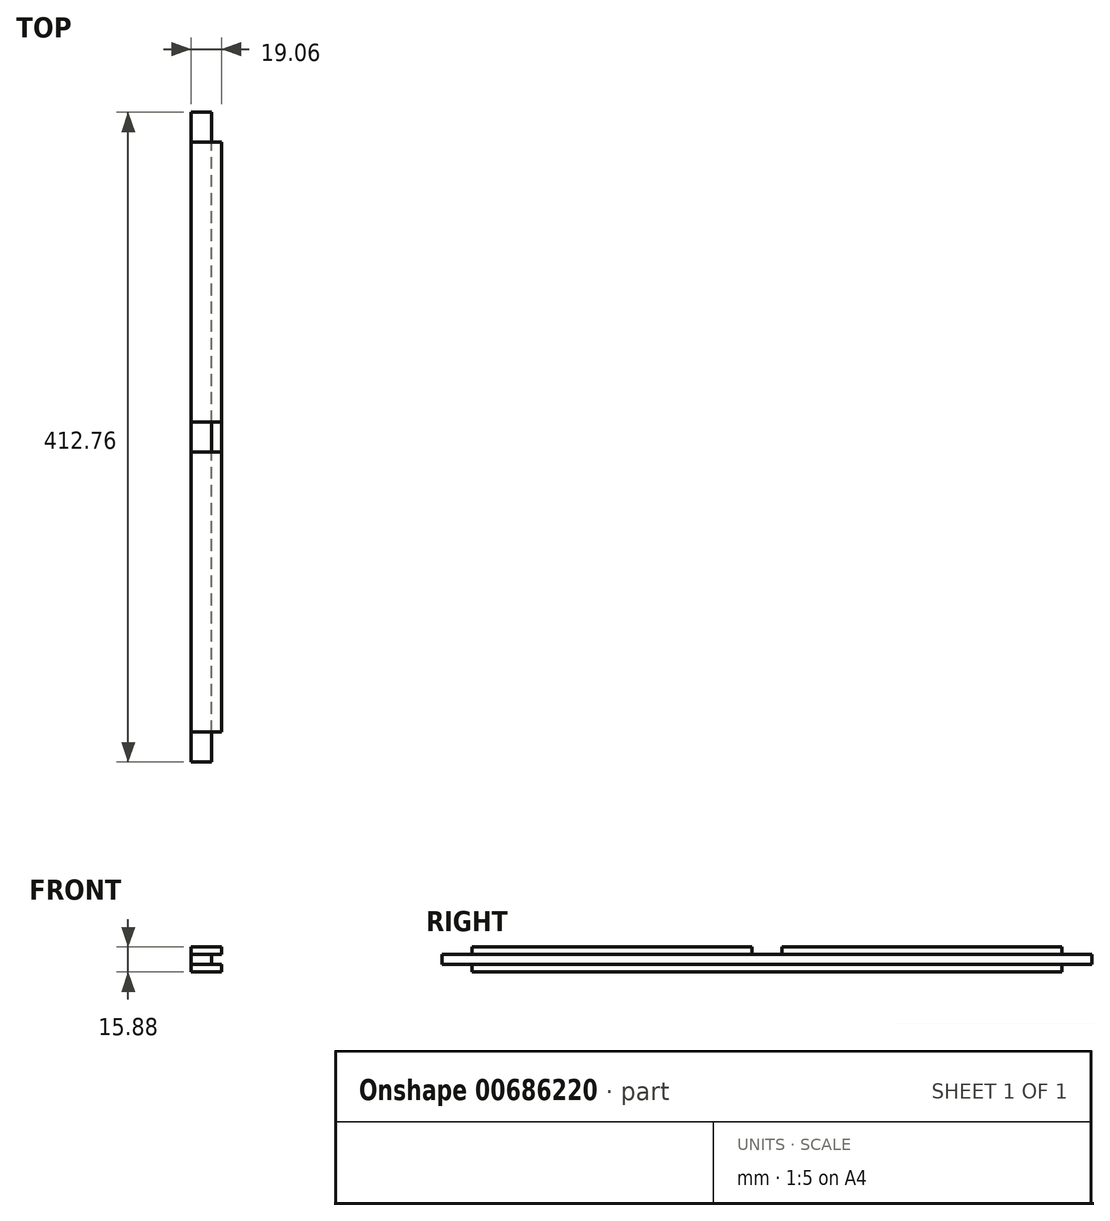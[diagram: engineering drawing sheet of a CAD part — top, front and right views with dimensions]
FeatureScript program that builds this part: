
annotation { "Feature Type Name" : "Feature", "Feature Type Description" : "" }
export const myFeature = defineFeature(function(context is Context, id is Id, definition is map)
    precondition{}
    {
        {
            var Q0;
            Q0=qCreatedBy(makeId("Front.planeOp"),FACE);
            var sketch = newSketch(context, id + "F0", { "sketchPlane" : qUnion([Q0])});
            skLineSegment(sketch, "E0.bottom", {"start": v(-9.53, 7.94) * mm, "end": v(9.52, 7.94) * mm});
            skLineSegment(sketch, "E0.top", {"start": v(-9.53, -7.94) * mm, "end": v(9.52, -7.94) * mm});
            skLineSegment(sketch, "E0.left", {"start": v(-9.53, 7.94) * mm, "end": v(-9.53, -7.94) * mm});
            skLineSegment(sketch, "E0.right", {"start": v(9.52, 7.94) * mm, "end": v(9.52, 3.18) * mm});
            skPoint(sketch, "E0.middle", {"position": v(0, 0) * mm});
            skLineSegment(sketch, "E1", {"start": v(9.52, 3.18) * mm, "end": v(3.17, 3.18) * mm});
            skLineSegment(sketch, "E2", {"start": v(3.17, 3.18) * mm, "end": v(3.17, -3.18) * mm});
            skLineSegment(sketch, "E3", {"start": v(3.17, -3.18) * mm, "end": v(9.52, -3.17) * mm});
            skLineSegment(sketch, "E4", {"start": v(0, 0) * mm, "end": v(3.17, 0) * mm, "construction": true});
            skLineSegment(sketch, "E5.trimOffspring", {"start": v(9.52, -3.17) * mm, "end": v(9.52, -7.94) * mm});
            skSolve(sketch);
        }
        {
            var Q0;
            Q0=qSketchRegion(id+"F0",true);
            extrude(context, id + "F1", {"entities" : qUnion([Q0]), "endBound" : BoundingType.SYMMETRIC, "depth" : 412.75 * mm, "offsetDistance" : 25.4 * mm});
        }
        {
            var Q0;
            Q0=qCreatedBy(makeId("Right.planeOp"),FACE);
            var sketch = newSketch(context, id + "F2", { "sketchPlane" : qUnion([Q0])});
            skLineSegment(sketch, "E6.bottom", {"start": v(-187.33, -3.17) * mm, "end": v(-206.38, -3.17) * mm, "construction": true});
            skLineSegment(sketch, "E6.top", {"start": v(-187.33, 3.18) * mm, "end": v(-206.38, 3.18) * mm, "construction": true});
            skLineSegment(sketch, "E6.left", {"start": v(-187.33, -3.17) * mm, "end": v(-187.33, 3.18) * mm, "construction": true});
            skLineSegment(sketch, "E6.right", {"start": v(-206.38, -3.17) * mm, "end": v(-206.38, 3.18) * mm, "construction": true});
            skLineSegment(sketch, "E7", {"start": v(0, 21.45) * mm, "end": v(0, -22.74) * mm, "construction": true});
            skLineSegment(sketch, "E8.MirrorCS", {"start": v(206.38, -3.17) * mm, "end": v(206.38, 3.18) * mm, "construction": true});
            skLineSegment(sketch, "E9.MirrorCS", {"start": v(187.33, -3.17) * mm, "end": v(187.33, 3.18) * mm, "construction": true});
            skLineSegment(sketch, "E10.MirrorCS", {"start": v(187.33, 3.18) * mm, "end": v(206.38, 3.18) * mm, "construction": true});
            skLineSegment(sketch, "E11.MirrorCS", {"start": v(187.33, -3.17) * mm, "end": v(206.38, -3.17) * mm, "construction": true});
            skLineSegment(sketch, "E12.bottom", {"start": v(-187.33, 3.18) * mm, "end": v(-206.38, 3.18) * mm});
            skLineSegment(sketch, "E12.top", {"start": v(-187.33, 7.94) * mm, "end": v(-206.38, 7.94) * mm});
            skLineSegment(sketch, "E12.left", {"start": v(-187.33, 3.18) * mm, "end": v(-187.33, 7.94) * mm});
            skLineSegment(sketch, "E12.right", {"start": v(-206.38, 3.18) * mm, "end": v(-206.38, 7.94) * mm});
            skLineSegment(sketch, "E13.bottom", {"start": v(-187.33, -3.17) * mm, "end": v(-206.38, -3.17) * mm});
            skLineSegment(sketch, "E13.top", {"start": v(-187.33, -7.94) * mm, "end": v(-206.38, -7.94) * mm});
            skLineSegment(sketch, "E13.left", {"start": v(-187.33, -3.17) * mm, "end": v(-187.33, -7.94) * mm});
            skLineSegment(sketch, "E13.right", {"start": v(-206.38, -3.17) * mm, "end": v(-206.38, -7.94) * mm});
            skLineSegment(sketch, "E14.bottom", {"start": v(187.33, 3.18) * mm, "end": v(206.38, 3.18) * mm});
            skLineSegment(sketch, "E14.top", {"start": v(187.33, 7.94) * mm, "end": v(206.38, 7.94) * mm});
            skLineSegment(sketch, "E14.left", {"start": v(187.33, 3.18) * mm, "end": v(187.33, 7.94) * mm});
            skLineSegment(sketch, "E14.right", {"start": v(206.38, 3.18) * mm, "end": v(206.38, 7.94) * mm});
            skLineSegment(sketch, "E15.bottom", {"start": v(187.33, -3.17) * mm, "end": v(206.38, -3.17) * mm});
            skLineSegment(sketch, "E15.top", {"start": v(187.33, -7.94) * mm, "end": v(206.38, -7.94) * mm});
            skLineSegment(sketch, "E15.left", {"start": v(187.33, -3.17) * mm, "end": v(187.33, -7.94) * mm});
            skLineSegment(sketch, "E15.right", {"start": v(206.38, -3.17) * mm, "end": v(206.38, -7.94) * mm});
            skLineSegment(sketch, "E16.bottom", {"start": v(-9.53, 7.94) * mm, "end": v(9.53, 7.94) * mm});
            skLineSegment(sketch, "E16.top", {"start": v(-9.52, 3.18) * mm, "end": v(9.53, 3.18) * mm});
            skLineSegment(sketch, "E16.left", {"start": v(-9.53, 7.94) * mm, "end": v(-9.53, 3.17) * mm});
            skLineSegment(sketch, "E16.right", {"start": v(9.52, 7.94) * mm, "end": v(9.52, 3.18) * mm});
            skSolve(sketch);
        }
        {
            var Q0;
            Q0=qSketchRegion(id+"F2",true);
            extrude(context, id + "F3", {"entities" : qUnion([Q0]), "operationType" : NewBodyOperationType.REMOVE, "endBound" : BoundingType.THROUGH_ALL, "oppositeDirection" : true, "depth" : 25.4 * mm, "offsetDistance" : 25.4 * mm, "hasSecondDirection" : true, "secondDirectionBound" : SecondDirectionBoundingType.THROUGH_ALL, "secondDirectionOppositeDirection" : false, "secondDirectionDepth" : 25.4 * mm});
        }
    });
